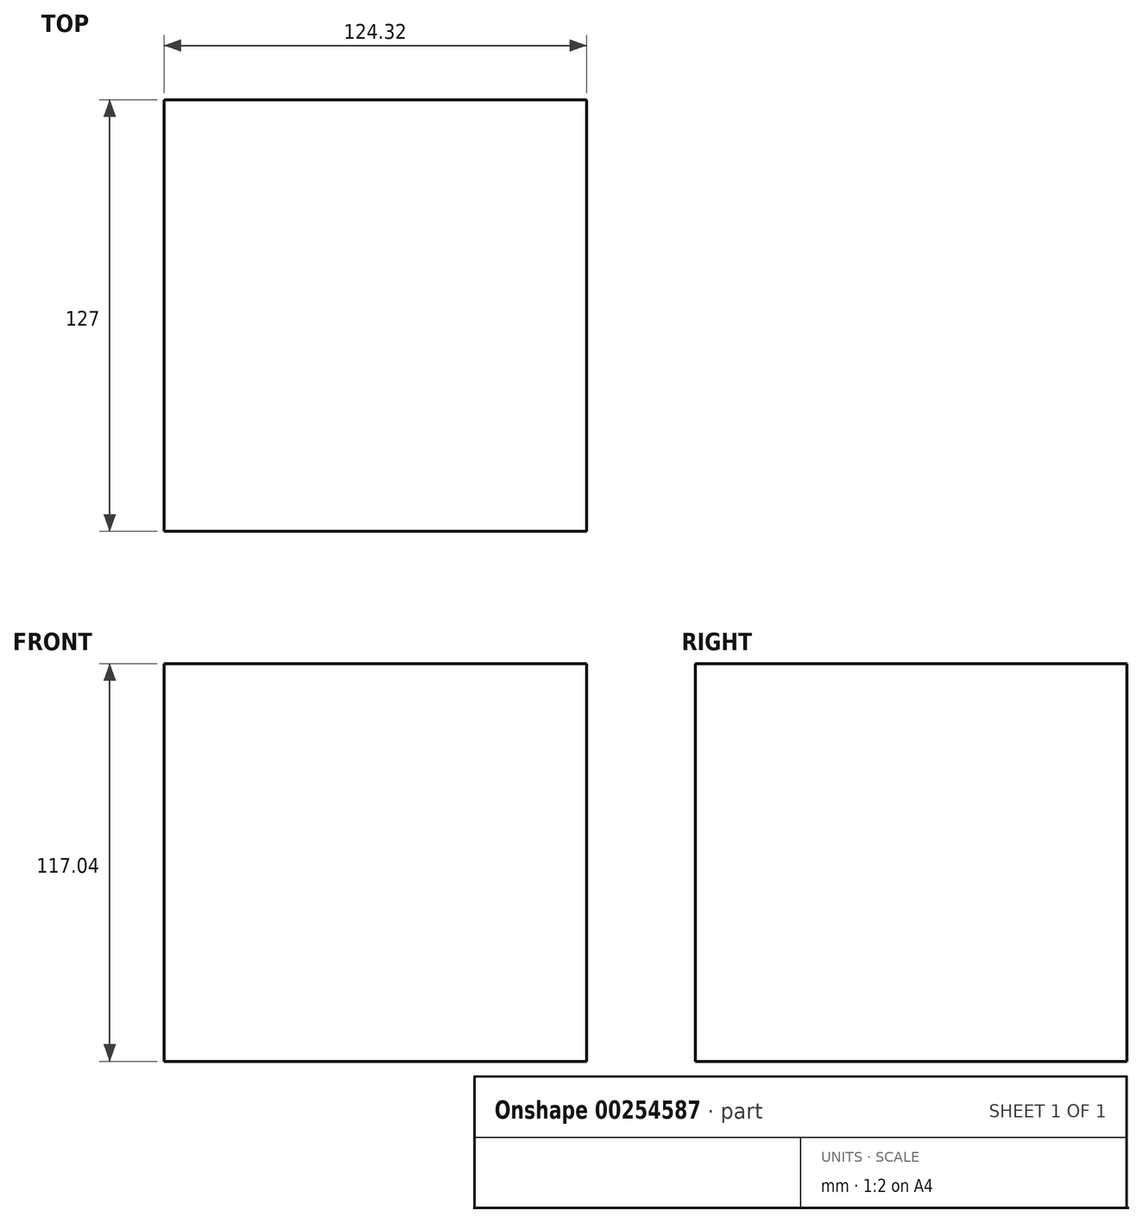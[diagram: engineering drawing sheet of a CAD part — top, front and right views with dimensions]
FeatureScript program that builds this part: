
annotation { "Feature Type Name" : "Feature", "Feature Type Description" : "" }
export const myFeature = defineFeature(function(context is Context, id is Id, definition is map)
    precondition{}
    {
        {
            var Q0;
            Q0=qCreatedBy(makeId("Front.planeOp"),FACE);
            var sketch = newSketch(context, id + "F0", { "sketchPlane" : qUnion([Q0])});
            skLineSegment(sketch, "E0.bottom", {"start": v(62.16, 58.52) * mm, "end": v(-62.16, 58.52) * mm});
            skLineSegment(sketch, "E0.top", {"start": v(62.16, -58.52) * mm, "end": v(-62.16, -58.52) * mm});
            skLineSegment(sketch, "E0.left", {"start": v(62.16, 58.52) * mm, "end": v(62.16, -58.52) * mm});
            skLineSegment(sketch, "E0.right", {"start": v(-62.16, 58.52) * mm, "end": v(-62.16, -58.52) * mm});
            skPoint(sketch, "E0.middle", {"position": v(0, 0) * mm});
            skSolve(sketch);
        }
        {
            var Q0;
            Q0 = qSketchRegion(id + "F0", true);
            extrude(context, id + "F1", {"entities" : qUnion([Q0]), "depth" : 127 * mm});
        }
    });
